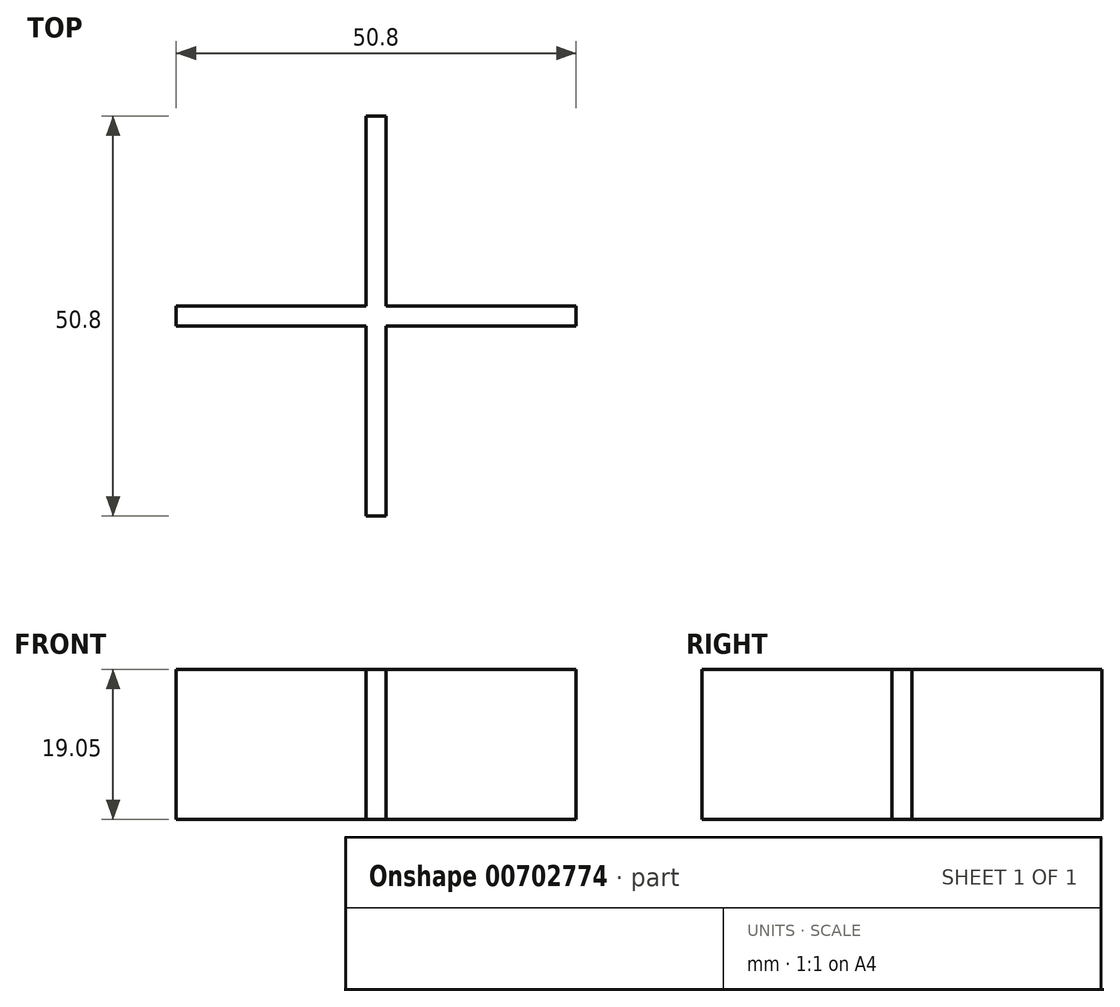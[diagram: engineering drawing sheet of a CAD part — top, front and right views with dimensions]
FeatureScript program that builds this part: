
annotation { "Feature Type Name" : "Feature", "Feature Type Description" : "" }
export const myFeature = defineFeature(function(context is Context, id is Id, definition is map)
    precondition{}
    {
        {
            var Q0;
            Q0=qCreatedBy(makeId("Top.planeOp"),FACE);
            var sketch = newSketch(context, id + "F0", { "sketchPlane" : qUnion([Q0])});
            skLineSegment(sketch, "E0.bottom", {"start": v(-3.96, 26.67) * mm, "end": v(-1.42, 26.67) * mm});
            skLineSegment(sketch, "E0.top", {"start": v(-3.96, -24.13) * mm, "end": v(-1.42, -24.13) * mm});
            skLineSegment(sketch, "E0.left", {"start": v(-3.96, 26.67) * mm, "end": v(-3.96, -24.13) * mm});
            skLineSegment(sketch, "E0.right", {"start": v(-1.42, 26.67) * mm, "end": v(-1.42, -24.13) * mm});
            skLineSegment(sketch, "E1.bottom", {"start": v(-28.1, 2.54) * mm, "end": v(22.7, 2.54) * mm});
            skLineSegment(sketch, "E1.top", {"start": v(-28.1, 0) * mm, "end": v(22.7, 0) * mm});
            skLineSegment(sketch, "E1.left", {"start": v(-28.1, 2.54) * mm, "end": v(-28.1, 0) * mm});
            skLineSegment(sketch, "E1.right", {"start": v(22.7, 2.54) * mm, "end": v(22.7, 0) * mm});
            skSolve(sketch);
        }
        {
            var Q0;
            Q0=qSketchRegion(id+"F0",true);
            extrude(context, id + "F1", {"entities" : qUnion([Q0]), "depth" : 19.05 * mm, "offsetDistance" : 25.4 * mm});
        }
    });
